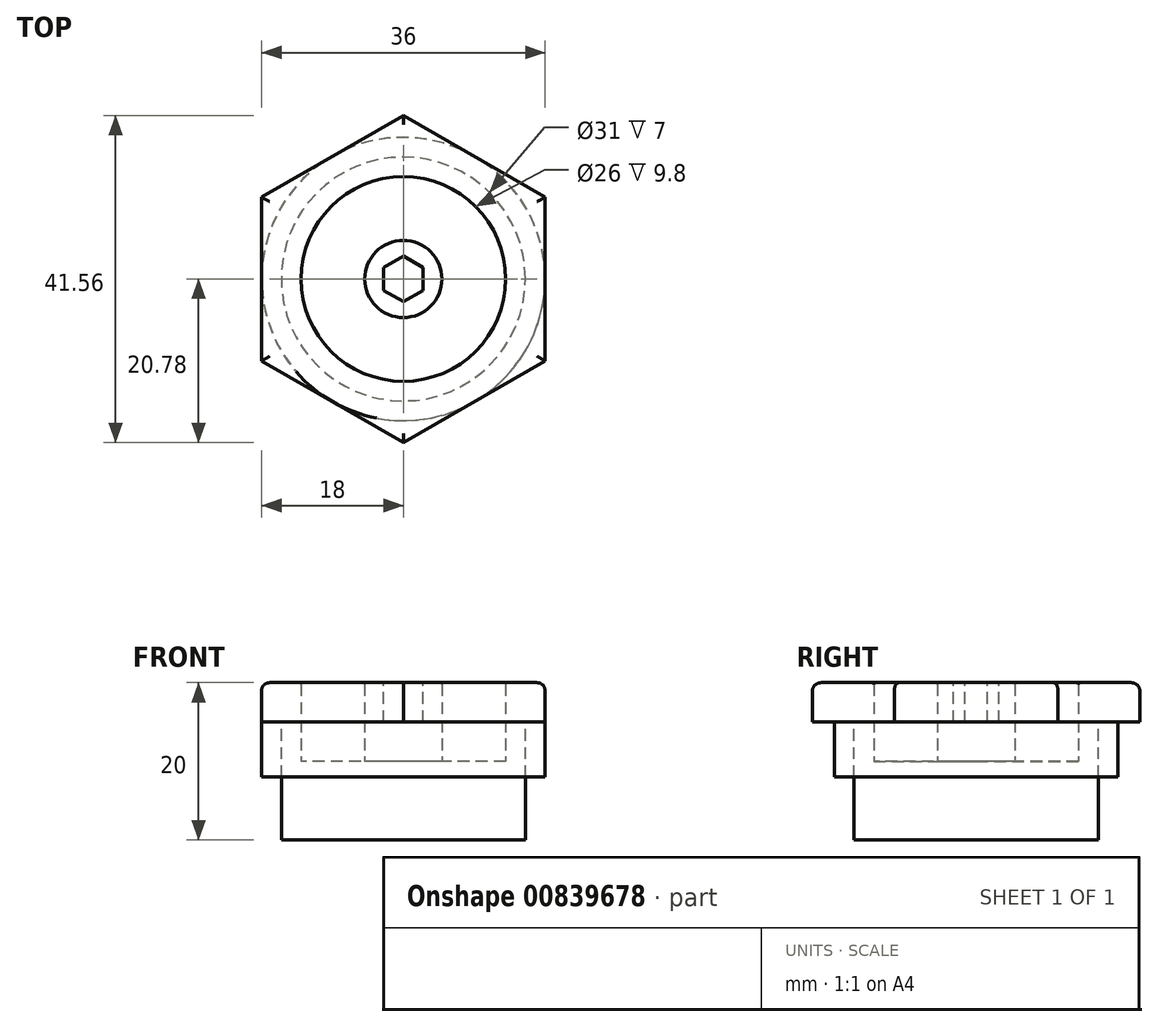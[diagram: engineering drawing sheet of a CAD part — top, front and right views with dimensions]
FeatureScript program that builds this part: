
annotation { "Feature Type Name" : "Feature", "Feature Type Description" : "" }
export const myFeature = defineFeature(function(context is Context, id is Id, definition is map)
    precondition{}
    {
        {
            var Q0;
            Q0=qCreatedBy(makeId("Top.planeOp"),FACE);
            var sketch = newSketch(context, id + "F0", { "sketchPlane" : qUnion([Q0])});
            skCircle(sketch, "E0", {"center": v(0, 0) * mm, "radius": 15.5 * mm});
            skCircle(sketch, "E1.cCircle", {"center": v(0, 0) * mm, "radius": 18 * mm, "construction": true});
            skLineSegment(sketch, "E1.0", {"start": v(18, 10.4) * mm, "end": v(18, -10.4) * mm});
            skLineSegment(sketch, "E1.1", {"start": v(18, -10.4) * mm, "end": v(0, -20.78) * mm});
            skLineSegment(sketch, "E1.2", {"start": v(0, -20.78) * mm, "end": v(-18, -10.4) * mm});
            skLineSegment(sketch, "E1.3", {"start": v(-18, -10.4) * mm, "end": v(-18, 10.4) * mm});
            skLineSegment(sketch, "E1.4", {"start": v(-18, 10.4) * mm, "end": v(0, 20.78) * mm});
            skLineSegment(sketch, "E1.5", {"start": v(0, 20.78) * mm, "end": v(18, 10.4) * mm});
            skPoint(sketch, "E1.0.midPoint", {"position": v(18, 0) * mm});
            skCircle(sketch, "E2", {"center": v(0, 0) * mm, "radius": 18 * mm});
            skCircle(sketch, "E3", {"center": v(0, 0) * mm, "radius": 13 * mm});
            skSolve(sketch);
        }
        {
            var Q0;
            Q0=makeQuery(id+"F0.imprint","IMPRINT",FACE,{"disambiguationData":[TD([[makeQuery(id+"F0.imprint","IMPRINT",EDGE,{"derivedFrom":sQuery(id+"F0.wireOp",EDGE,"E0")}),-1.0]])]});
            var Q1;
            {var subQ0=sQuery(id+"F0.wireOp",EDGE,"E1.5");var subQ1=sQuery(id+"F0.wireOp",EDGE,"1b6a4559-1ce8-44c5-8ccb-9f9d9290bb9e.0");var subQ2=makeQuery(id+"F0.imprint","INTERSECT",VERTEX,{"disambiguationData":[OD(1.0)],"derivedFrom":[subQ1,subQ0]});Q1=makeQuery(id+"F0.imprint","IMPRINT",FACE,{"disambiguationData":[TD([[makeQuery(id+"F0.imprint","IMPRINT",EDGE,{"disambiguationData":[TD([[subQ2,-1.0]])],"derivedFrom":subQ1}),-1.0]])]});}
            var Q2;
            {var subQ0=sQuery(id+"F0.wireOp",EDGE,"E1.4");var subQ1=sQuery(id+"F0.wireOp",EDGE,"1b6a4559-1ce8-44c5-8ccb-9f9d9290bb9e.0");var subQ2=makeQuery(id+"F0.imprint","INTERSECT",VERTEX,{"disambiguationData":[OD(1.0)],"derivedFrom":[subQ1,subQ0]});Q2=makeQuery(id+"F0.imprint","IMPRINT",FACE,{"disambiguationData":[TD([[makeQuery(id+"F0.imprint","IMPRINT",EDGE,{"disambiguationData":[TD([[subQ2,-1.0]])],"derivedFrom":subQ1}),-1.0]])]});}
            var Q3;
            {var subQ0=sQuery(id+"F0.wireOp",EDGE,"E1.5");var subQ1=sQuery(id+"F0.wireOp",EDGE,"1b6a4559-1ce8-44c5-8ccb-9f9d9290bb9e.0");var subQ2=makeQuery(id+"F0.imprint","INTERSECT",VERTEX,{"disambiguationData":[OD(0.0)],"derivedFrom":[subQ1,subQ0]});Q3=makeQuery(id+"F0.imprint","IMPRINT",FACE,{"disambiguationData":[TD([[makeQuery(id+"F0.imprint","IMPRINT",EDGE,{"disambiguationData":[TD([[subQ2,1.0]])],"derivedFrom":subQ1}),-1.0]])]});}
            var Q4;
            {var subQ0=sQuery(id+"F0.wireOp",EDGE,"E1.1");var subQ1=sQuery(id+"F0.wireOp",EDGE,"1b6a4559-1ce8-44c5-8ccb-9f9d9290bb9e.0");var subQ2=makeQuery(id+"F0.imprint","INTERSECT",VERTEX,{"disambiguationData":[OD(1.0)],"derivedFrom":[subQ1,subQ0]});Q4=makeQuery(id+"F0.imprint","IMPRINT",FACE,{"disambiguationData":[TD([[makeQuery(id+"F0.imprint","IMPRINT",EDGE,{"disambiguationData":[TD([[subQ2,-1.0]])],"derivedFrom":subQ1}),-1.0]])]});}
            var Q5;
            {var subQ0=sQuery(id+"F0.wireOp",EDGE,"E1.2");var subQ1=sQuery(id+"F0.wireOp",EDGE,"1b6a4559-1ce8-44c5-8ccb-9f9d9290bb9e.0");var subQ2=makeQuery(id+"F0.imprint","INTERSECT",VERTEX,{"disambiguationData":[OD(1.0)],"derivedFrom":[subQ1,subQ0]});Q5=makeQuery(id+"F0.imprint","IMPRINT",FACE,{"disambiguationData":[TD([[makeQuery(id+"F0.imprint","IMPRINT",EDGE,{"disambiguationData":[TD([[subQ2,-1.0]])],"derivedFrom":subQ1}),-1.0]])]});}
            var Q6;
            {var subQ0=sQuery(id+"F0.wireOp",EDGE,"E1.3");var subQ1=sQuery(id+"F0.wireOp",EDGE,"1b6a4559-1ce8-44c5-8ccb-9f9d9290bb9e.0");var subQ2=makeQuery(id+"F0.imprint","INTERSECT",VERTEX,{"disambiguationData":[OD(1.0)],"derivedFrom":[subQ1,subQ0]});Q6=makeQuery(id+"F0.imprint","IMPRINT",FACE,{"disambiguationData":[TD([[makeQuery(id+"F0.imprint","IMPRINT",EDGE,{"disambiguationData":[TD([[subQ2,-1.0]])],"derivedFrom":subQ1}),-1.0]])]});}
            var Q7;
            {var subQ0=sQuery(id+"F0.wireOp",EDGE,"E1.5");var subQ1=sQuery(id+"F0.wireOp",EDGE,"E1.4");var subQ2=makeQuery(id+"F0.imprint","INTERSECT",VERTEX,{"derivedFrom":[subQ1,subQ0]});Q7=makeQuery(id+"F0.imprint","IMPRINT",FACE,{"disambiguationData":[TD([[makeQuery(id+"F0.imprint","IMPRINT",EDGE,{"disambiguationData":[TD([[subQ2,1.0]])],"derivedFrom":subQ1}),-1.0]])]});}
            var Q8;
            {var subQ0=sQuery(id+"F0.wireOp",EDGE,"E1.5");var subQ1=sQuery(id+"F0.wireOp",EDGE,"E1.0");var subQ2=makeQuery(id+"F0.imprint","INTERSECT",VERTEX,{"derivedFrom":[subQ1,subQ0]});Q8=makeQuery(id+"F0.imprint","IMPRINT",FACE,{"disambiguationData":[TD([[makeQuery(id+"F0.imprint","IMPRINT",EDGE,{"disambiguationData":[TD([[subQ2,-1.0]])],"derivedFrom":subQ1}),-1.0]])]});}
            var Q9;
            {var subQ0=sQuery(id+"F0.wireOp",EDGE,"E1.4");var subQ1=sQuery(id+"F0.wireOp",EDGE,"E1.3");var subQ2=makeQuery(id+"F0.imprint","INTERSECT",VERTEX,{"derivedFrom":[subQ1,subQ0]});Q9=makeQuery(id+"F0.imprint","IMPRINT",FACE,{"disambiguationData":[TD([[makeQuery(id+"F0.imprint","IMPRINT",EDGE,{"disambiguationData":[TD([[subQ2,1.0]])],"derivedFrom":subQ1}),-1.0]])]});}
            var Q10;
            {var subQ0=sQuery(id+"F0.wireOp",EDGE,"E1.3");var subQ1=sQuery(id+"F0.wireOp",EDGE,"E1.2");var subQ2=makeQuery(id+"F0.imprint","INTERSECT",VERTEX,{"derivedFrom":[subQ1,subQ0]});Q10=makeQuery(id+"F0.imprint","IMPRINT",FACE,{"disambiguationData":[TD([[makeQuery(id+"F0.imprint","IMPRINT",EDGE,{"disambiguationData":[TD([[subQ2,1.0]])],"derivedFrom":subQ1}),-1.0]])]});}
            var Q11;
            {var subQ0=sQuery(id+"F0.wireOp",EDGE,"E1.2");var subQ1=sQuery(id+"F0.wireOp",EDGE,"E1.1");var subQ2=makeQuery(id+"F0.imprint","INTERSECT",VERTEX,{"derivedFrom":[subQ1,subQ0]});Q11=makeQuery(id+"F0.imprint","IMPRINT",FACE,{"disambiguationData":[TD([[makeQuery(id+"F0.imprint","IMPRINT",EDGE,{"disambiguationData":[TD([[subQ2,1.0]])],"derivedFrom":subQ1}),-1.0]])]});}
            var Q12;
            {var subQ0=sQuery(id+"F0.wireOp",EDGE,"E1.1");var subQ1=sQuery(id+"F0.wireOp",EDGE,"E1.0");var subQ2=makeQuery(id+"F0.imprint","INTERSECT",VERTEX,{"derivedFrom":[subQ1,subQ0]});Q12=makeQuery(id+"F0.imprint","IMPRINT",FACE,{"disambiguationData":[TD([[makeQuery(id+"F0.imprint","IMPRINT",EDGE,{"disambiguationData":[TD([[subQ2,1.0]])],"derivedFrom":subQ1}),-1.0]])]});}
            var Q13;
            Q13=makeQuery(id+"F0.imprint","IMPRINT",FACE,{"disambiguationData":[TD([[makeQuery(id+"F0.imprint","IMPRINT",EDGE,{"derivedFrom":sQuery(id+"F0.wireOp",EDGE,"E0")}),1.0]])]});
            extrude(context, id + "F1", {"entities" : qUnion([Q0, Q1, Q2, Q3, Q4, Q5, Q6, Q7, Q8, Q9, Q10, Q11, Q12, Q13]), "depth" : 5 * mm, "offsetDistance" : 25 * mm});
        }
        {
            var Q0;
            Q0=makeQuery(id+"F1.opExtrude","CAP_EDGE",EDGE,{"disambiguationData":[OSD([sQuery(id+"F0.wireOp",EDGE,"E1.3")])],"isStart":false});
            var Q1;
            Q1=makeQuery(id+"F1.opExtrude","CAP_EDGE",EDGE,{"disambiguationData":[OSD([sQuery(id+"F0.wireOp",EDGE,"E1.4")])],"isStart":false});
            var Q2;
            Q2=makeQuery(id+"F1.opExtrude","CAP_EDGE",EDGE,{"disambiguationData":[OSD([sQuery(id+"F0.wireOp",EDGE,"E1.5")])],"isStart":false});
            var Q3;
            Q3=makeQuery(id+"F1.opExtrude","CAP_EDGE",EDGE,{"disambiguationData":[OSD([sQuery(id+"F0.wireOp",EDGE,"E1.0")])],"isStart":false});
            var Q4;
            Q4=makeQuery(id+"F1.opExtrude","CAP_EDGE",EDGE,{"disambiguationData":[OSD([sQuery(id+"F0.wireOp",EDGE,"E1.1")])],"isStart":false});
            var Q5;
            Q5=makeQuery(id+"F1.opExtrude","CAP_EDGE",EDGE,{"disambiguationData":[OSD([sQuery(id+"F0.wireOp",EDGE,"E1.2")])],"isStart":false});
            fillet(context, id + "F2", {"entities" : qUnion([Q0, Q1, Q2, Q3, Q4, Q5]), "radius" : 1 * mm, "tangentPropagation" : true, "allowEdgeOverflow" : false});
        }
        {
            var Q0;
            Q0=makeQuery(id+"F0.imprint","IMPRINT",FACE,{"disambiguationData":[TD([[makeQuery(id+"F0.imprint","IMPRINT",EDGE,{"derivedFrom":sQuery(id+"F0.wireOp",EDGE,"E3")}),1.0]])]});
            var Q1;
            Q1=makeQuery(id+"F0.imprint","IMPRINT",FACE,{"disambiguationData":[TD([[makeQuery(id+"F0.imprint","IMPRINT",EDGE,{"derivedFrom":sQuery(id+"F0.wireOp",EDGE,"E0")}),1.0]])]});
            extrude(context, id + "F3", {"entities" : qUnion([Q0, Q1]), "operationType" : NewBodyOperationType.ADD, "oppositeDirection" : true, "depth" : 15 * mm, "offsetDistance" : 25 * mm});
        }
        {
            var Q0;
            Q0=makeQuery(id+"F0.imprint","IMPRINT",FACE,{"disambiguationData":[TD([[makeQuery(id+"F0.imprint","IMPRINT",EDGE,{"derivedFrom":sQuery(id+"F0.wireOp",EDGE,"E3")}),1.0]])]});
            extrude(context, id + "F4", {"entities" : qUnion([Q0]), "operationType" : NewBodyOperationType.REMOVE, "oppositeDirection" : true, "depth" : 5 * mm, "offsetDistance" : 25 * mm});
        }
        {
            var Q0;
            Q0=makeQuery(id+"F4.boolean.opBoolean","COPY",FACE,{"derivedFrom":makeQuery(id+"F4.opExtrude","CAP_FACE",FACE,{"disambiguationData":[OSD([sQuery(id+"F0.wireOp",EDGE,"E3")])],"isStart":false})});
            var sketch = newSketch(context, id + "F5", { "sketchPlane" : qUnion([Q0])});
            skPoint(sketch, "E4.0", {"position": v(0, 0) * mm});
            skCircle(sketch, "E5", {"center": v(0, 0) * mm, "radius": 4.9 * mm});
            skSolve(sketch);
        }
        {
            var Q0;
            Q0=makeQuery(id+"F5.imprint","IMPRINT",FACE,{"disambiguationData":[TD([[makeQuery(id+"F5.imprint","IMPRINT",EDGE,{"derivedFrom":sQuery(id+"F5.wireOp",EDGE,"E5")}),1.0]])]});
            var Q1;
            Q1=makeQuery(id+"F1.opExtrude","CAP_FACE",FACE,{"disambiguationData":[OSD([sQuery(id+"F0.wireOp",EDGE,"E1.0"),sQuery(id+"F0.wireOp",EDGE,"E1.1"),sQuery(id+"F0.wireOp",EDGE,"E1.2"),sQuery(id+"F0.wireOp",EDGE,"E1.3"),sQuery(id+"F0.wireOp",EDGE,"E1.4"),sQuery(id+"F0.wireOp",EDGE,"E1.5"),sQuery(id+"F0.wireOp",EDGE,"E3")])],"isStart":false});
            extrude(context, id + "F6", {"entities" : qUnion([Q0]), "operationType" : NewBodyOperationType.ADD, "endBound" : BoundingType.UP_TO_SURFACE, "depth" : 25 * mm, "endBoundEntityFace" : qUnion([Q1]), "offsetDistance" : 25 * mm});
        }
        {
            var Q0;
            Q0=makeQuery(id+"F6.opExtrude","CAP_FACE",FACE,{"disambiguationData":[OSD([sQuery(id+"F5.wireOp",EDGE,"E5")])],"isStart":false});
            var sketch = newSketch(context, id + "F7", { "sketchPlane" : qUnion([Q0])});
            skPoint(sketch, "E6.0", {"position": v(0, 0) * mm});
            skCircle(sketch, "E7.cCircle", {"center": v(0, 0) * mm, "radius": 2.5 * mm, "construction": true});
            skLineSegment(sketch, "E7.0", {"start": v(-2.5, -1.44) * mm, "end": v(-2.5, 1.44) * mm});
            skLineSegment(sketch, "E7.1", {"start": v(-2.5, 1.44) * mm, "end": v(0, 2.89) * mm});
            skLineSegment(sketch, "E7.2", {"start": v(0, 2.89) * mm, "end": v(2.5, 1.44) * mm});
            skLineSegment(sketch, "E7.3", {"start": v(2.5, 1.44) * mm, "end": v(2.5, -1.44) * mm});
            skLineSegment(sketch, "E7.4", {"start": v(2.5, -1.44) * mm, "end": v(0, -2.89) * mm});
            skLineSegment(sketch, "E7.5", {"start": v(0, -2.89) * mm, "end": v(-2.5, -1.44) * mm});
            skPoint(sketch, "E7.0.midPoint", {"position": v(-2.5, 0) * mm});
            skSolve(sketch);
        }
        {
            var Q0;
            Q0=makeQuery(id+"F7.imprint","IMPRINT",FACE,{"disambiguationData":[TD([[makeQuery(id+"F7.imprint","IMPRINT",EDGE,{"derivedFrom":sQuery(id+"F7.wireOp",EDGE,"E7.0")}),-1.0]])]});
            extrude(context, id + "F8", {"entities" : qUnion([Q0]), "operationType" : NewBodyOperationType.REMOVE, "oppositeDirection" : true, "depth" : 5 * mm, "offsetDistance" : 25 * mm});
        }
        {
            var Q0;
            Q0=makeQuery(id+"F6.opExtrude","CAP_EDGE",EDGE,{"disambiguationData":[OSD([sQuery(id+"F5.wireOp",EDGE,"E5")])],"isStart":false});
            var Q1;
            Q1=makeQuery(id+"F1.opExtrude","CAP_EDGE",EDGE,{"disambiguationData":[OSD([sQuery(id+"F0.wireOp",EDGE,"E3")])],"isStart":false});
            var Q2;
            Q2=makeQuery(id+"F8.boolean.opBoolean","COPY",EDGE,{"derivedFrom":makeQuery(id+"F8.opExtrude","CAP_EDGE",EDGE,{"disambiguationData":[OSD([sQuery(id+"F7.wireOp",EDGE,"E7.1")])],"isStart":true})});
            var Q3;
            Q3=makeQuery(id+"F8.boolean.opBoolean","COPY",EDGE,{"derivedFrom":makeQuery(id+"F8.opExtrude","CAP_EDGE",EDGE,{"disambiguationData":[OSD([sQuery(id+"F7.wireOp",EDGE,"E7.2")])],"isStart":true})});
            var Q4;
            Q4=makeQuery(id+"F8.boolean.opBoolean","COPY",EDGE,{"derivedFrom":makeQuery(id+"F8.opExtrude","CAP_EDGE",EDGE,{"disambiguationData":[OSD([sQuery(id+"F7.wireOp",EDGE,"E7.3")])],"isStart":true})});
            var Q5;
            Q5=makeQuery(id+"F8.boolean.opBoolean","COPY",EDGE,{"derivedFrom":makeQuery(id+"F8.opExtrude","CAP_EDGE",EDGE,{"disambiguationData":[OSD([sQuery(id+"F7.wireOp",EDGE,"E7.4")])],"isStart":true})});
            var Q6;
            Q6=makeQuery(id+"F8.boolean.opBoolean","COPY",EDGE,{"derivedFrom":makeQuery(id+"F8.opExtrude","CAP_EDGE",EDGE,{"disambiguationData":[OSD([sQuery(id+"F7.wireOp",EDGE,"E7.5")])],"isStart":true})});
            var Q7;
            Q7=makeQuery(id+"F8.boolean.opBoolean","COPY",EDGE,{"derivedFrom":makeQuery(id+"F8.opExtrude","CAP_EDGE",EDGE,{"disambiguationData":[OSD([sQuery(id+"F7.wireOp",EDGE,"E7.0")])],"isStart":true})});
            fillet(context, id + "F9", {"entities" : qUnion([Q0, Q1, Q2, Q3, Q4, Q5, Q6, Q7]), "radius" : 0.2 * mm, "tangentPropagation" : true, "allowEdgeOverflow" : false});
        }
        {
            var Q0;
            Q0=makeQuery(id+"F0.imprint","IMPRINT",FACE,{"disambiguationData":[TD([[makeQuery(id+"F0.imprint","IMPRINT",EDGE,{"derivedFrom":sQuery(id+"F0.wireOp",EDGE,"E0")}),-1.0]])]});
            extrude(context, id + "F10", {"entities" : qUnion([Q0]), "oppositeDirection" : true, "depth" : 7 * mm, "offsetDistance" : 25 * mm});
        }
    });
